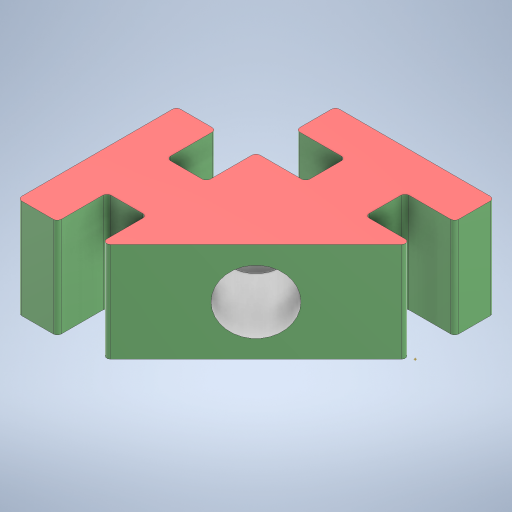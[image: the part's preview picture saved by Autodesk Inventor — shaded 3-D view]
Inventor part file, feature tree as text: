
AUTODESK INVENTOR PART (.ipt)
format: ipt  version: 2023 (Build 270158000, 158)  size: 277,504 bytes
history: native  units: in
note: dims shown in document units (in); Inventor stores cm internally (conversion verified against a paired STEP export)
features: other x5, sketch x1, extrude x1, projected_geometry x1
ambient origin geometry x8: Origin, YZ Plane, XZ Plane, XY Plane, X Axis, Y Axis, Z Axis, Center Point
bodies: Body1 (feature_tree)
feature tree (8):
  other  "FlexPart.ipt"
  sketch  "Sketch1"  dims[d0=0.3937in d1=0.126in d2=0.1575in d3=0.0in]
  other  "Work Point1"
  extrude  "Extrusion1"  Depth=0.1575in
  other  "PLA2::FlexPart.ipt"
  other  "TaggingFeature1"
  projected_geometry  "Projected Loop1"
  other  "PLA2"
